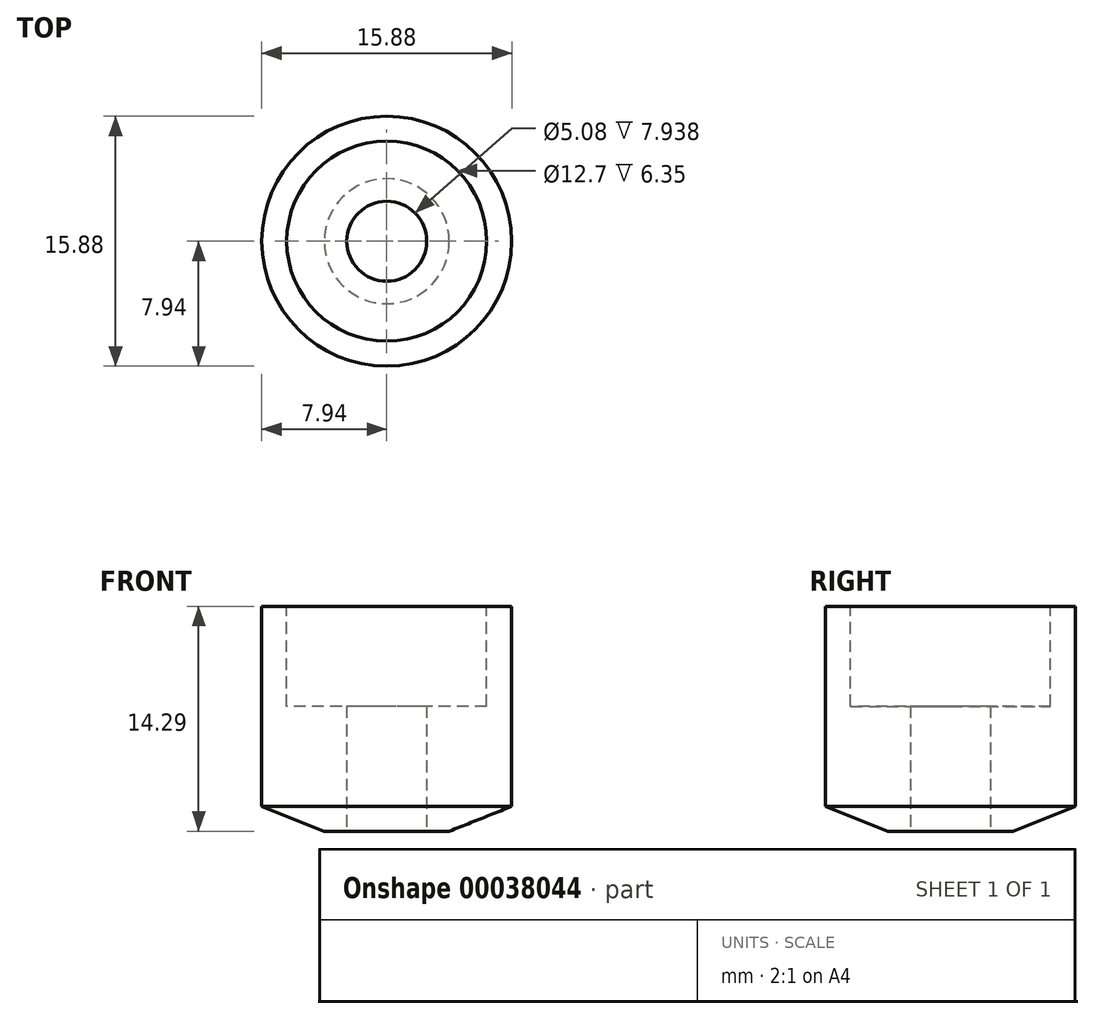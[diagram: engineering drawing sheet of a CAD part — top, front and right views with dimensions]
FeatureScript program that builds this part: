
annotation { "Feature Type Name" : "Feature", "Feature Type Description" : "" }
export const myFeature = defineFeature(function(context is Context, id is Id, definition is map)
    precondition{}
    {
        {
            var Q0;
            Q0=qCreatedBy(makeId("Top.planeOp"),FACE);
            var sketch = newSketch(context, id + "F0", { "sketchPlane" : qUnion([Q0])});
            skCircle(sketch, "E0", {"center": v(0, 0) * mm, "radius": 7.94 * mm});
            skCircle(sketch, "E1", {"center": v(0, 0) * mm, "radius": 2.54 * mm});
            skSolve(sketch);
        }
        {
            var Q0;
            Q0 = qSketchRegion(id + "F0", true);
            extrude(context, id + "F1", {"entities" : qUnion([Q0]), "depth" : 14.29 * mm});
        }
        {
            var Q0;
            Q0=makeQuery(id+"F1.opExtrude","CAP_EDGE",EDGE,{"disambiguationData":[OSD([sQuery(id+"F0.wireOp",EDGE,"E0")])],"isStart":true});
            chamfer(context, id + "F2", {"entities" : qUnion([Q0]), "chamferType" : ChamferType.TWO_OFFSETS, "width1" : 1.59 * mm, "oppositeDirection" : false, "width2" : 3.97 * mm, "tangentPropagation" : true});
        }
        {
            var Q0;
            Q0=makeQuery(id+"F1.opExtrude","CAP_FACE",FACE,{"disambiguationData":[OSD([sQuery(id+"F0.wireOp",EDGE,"E0"),sQuery(id+"F0.wireOp",EDGE,"E1")])],"isStart":false});
            var sketch = newSketch(context, id + "F3", { "sketchPlane" : qUnion([Q0])});
            skCircle(sketch, "E2", {"center": v(0, 0) * mm, "radius": 6.35 * mm});
            skCircle(sketch, "E3", {"center": v(0, 0) * mm, "radius": 2.54 * mm});
            skSolve(sketch);
        }
        {
            var Q0;
            Q0 = qSketchRegion(id + "F3", true);
            extrude(context, id + "F4", {"entities" : qUnion([Q0]), "operationType" : NewBodyOperationType.REMOVE, "oppositeDirection" : true, "depth" : 6.35 * mm});
        }
    });
